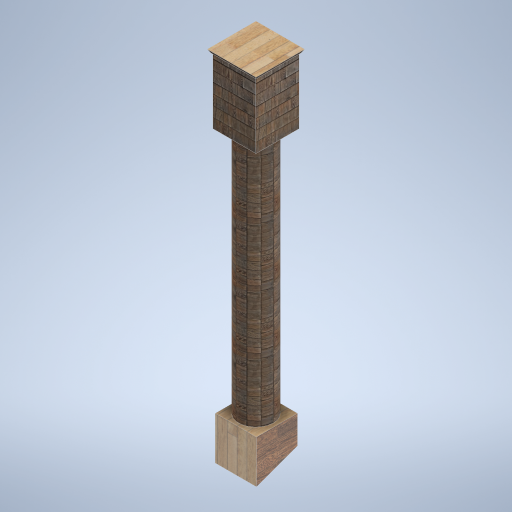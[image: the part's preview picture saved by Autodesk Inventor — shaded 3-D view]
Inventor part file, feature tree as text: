
AUTODESK INVENTOR PART (.ipt)
format: ipt  version: 2024.2 (Build 282272000, 272)  size: 353,280 bytes
history: native  units: in
note: dims shown in document units (in); Inventor stores cm internally (conversion verified against a paired STEP export)
features: sketch x5, other x3, plane x1
ambient origin geometry x8: Origin, YZ Plane, XZ Plane, XY Plane, X Axis, Y Axis, Z Axis, Center Point
bodies: Solid1 (feature_tree)
feature tree (9):
  other  "side_pillar_01.ipt"
  other  "Solid1::side_pillar_01.ipt"
  other  "TaggingFeature1"
  sketch  "Sketch1"  dims[d0=0.3937in]
  sketch  "Sketch2"
  sketch  "Sketch3"
  sketch  "Sketch4"
  sketch  "Sketch5"
  plane  "Work Plane3"
